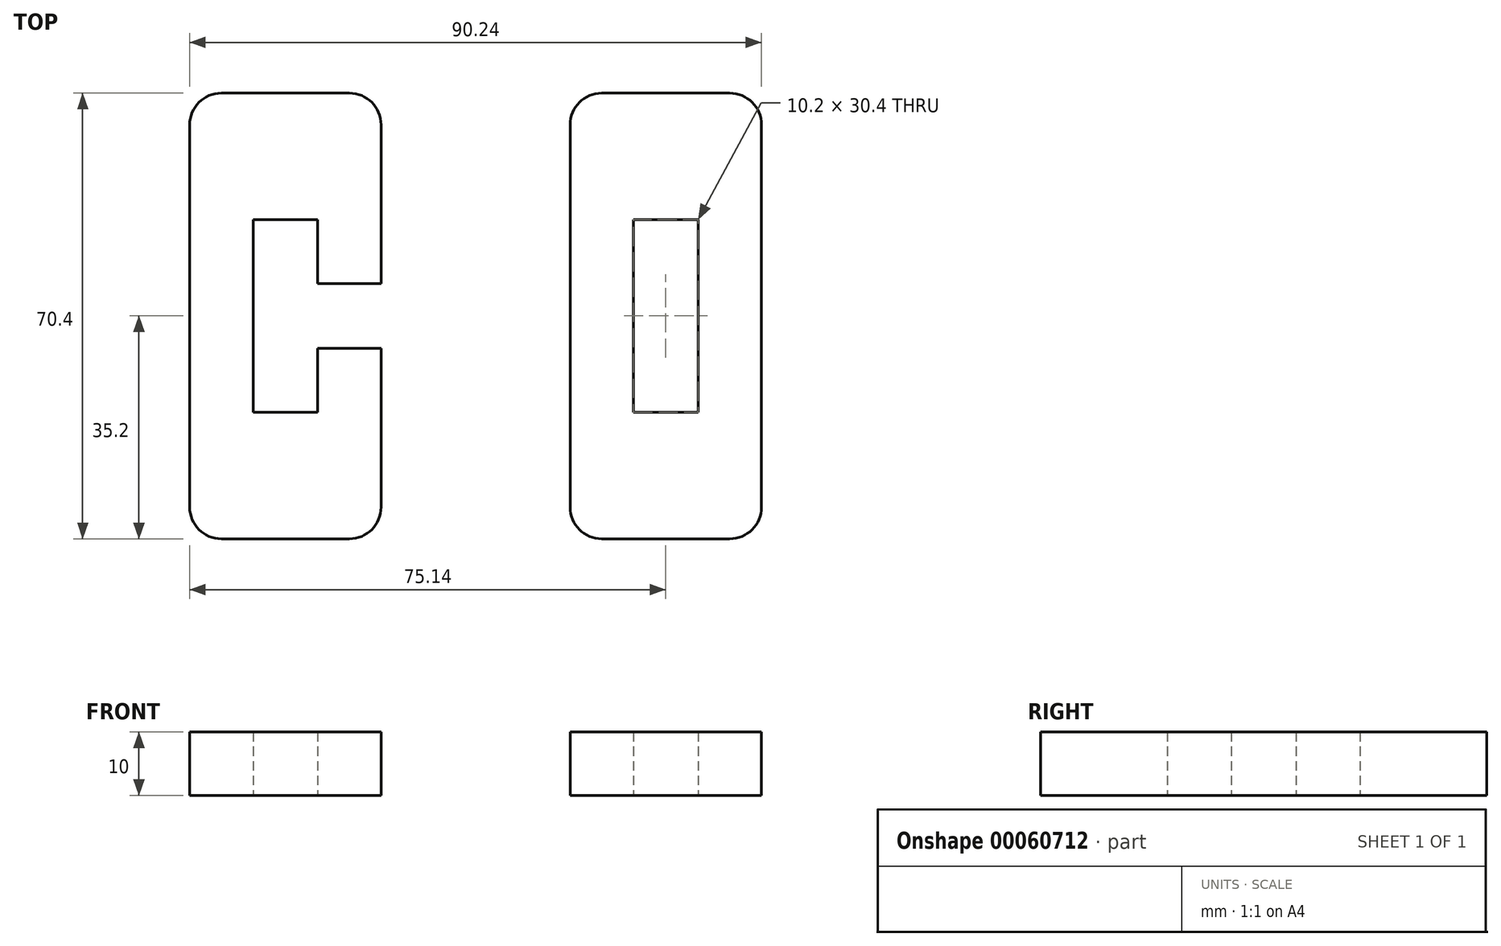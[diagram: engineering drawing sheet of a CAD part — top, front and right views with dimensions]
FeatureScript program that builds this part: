
annotation { "Feature Type Name" : "Feature", "Feature Type Description" : "" }
export const myFeature = defineFeature(function(context is Context, id is Id, definition is map)
    precondition{}
    {
        {
            var Q0;
            Q0=qCreatedBy(makeId("Top.planeOp"),FACE);
            var sketch = newSketch(context, id + "F0", { "sketchPlane" : qUnion([Q0])});
            skLineSegment(sketch, "E0.rect.bottom", {"start": v(-5.1, 15.2) * mm, "end": v(5.1, 15.2) * mm});
            skLineSegment(sketch, "E0.rect.top", {"start": v(-5.1, -15.2) * mm, "end": v(5.1, -15.2) * mm});
            skLineSegment(sketch, "E0.rect.left", {"start": v(-5.1, 15.2) * mm, "end": v(-5.1, -15.2) * mm});
            skLineSegment(sketch, "E0.rect.right", {"start": v(5.1, 15.2) * mm, "end": v(5.1, -15.2) * mm});
            skPoint(sketch, "E0.rect.middle", {"position": v(0, 0) * mm});
            skLineSegment(sketch, "E1.0", {"start": v(-10.1, 35.2) * mm, "end": v(10.1, 35.2) * mm});
            skLineSegment(sketch, "E1.1", {"start": v(-15.1, 30.2) * mm, "end": v(-15.1, -30.2) * mm});
            skLineSegment(sketch, "E1.2", {"start": v(-10.1, -35.2) * mm, "end": v(10.1, -35.2) * mm});
            skLineSegment(sketch, "E1.3", {"start": v(15.1, 30.2) * mm, "end": v(15.1, -30.2) * mm});
            skPoint(sketch, "E2", {"position": v(-60.04, 0) * mm});
            skLineSegment(sketch, "E3.rect.bottom", {"start": v(-65.14, 15.2) * mm, "end": v(-54.94, 15.2) * mm});
            skLineSegment(sketch, "E3.rect.top", {"start": v(-65.14, -15.2) * mm, "end": v(-54.94, -15.2) * mm});
            skLineSegment(sketch, "E3.rect.left", {"start": v(-65.14, 15.2) * mm, "end": v(-65.14, -15.2) * mm});
            skLineSegment(sketch, "E3.rect.right", {"start": v(-54.94, 15.2) * mm, "end": v(-54.94, -15.2) * mm});
            skLineSegment(sketch, "E4.0", {"start": v(-70.14, 35.2) * mm, "end": v(-49.94, 35.2) * mm});
            skLineSegment(sketch, "E4.1", {"start": v(-75.14, 30.2) * mm, "end": v(-75.14, -30.2) * mm});
            skLineSegment(sketch, "E4.2", {"start": v(-70.14, -35.2) * mm, "end": v(-49.94, -35.2) * mm});
            skLineSegment(sketch, "E4.3", {"start": v(-44.94, 30.2) * mm, "end": v(-44.94, -30.2) * mm});
            skLineSegment(sketch, "E5", {"start": v(-44.94, 0) * mm, "end": v(-54.94, 0) * mm});
            skLineSegment(sketch, "E6.0", {"start": v(-44.94, -5.1) * mm, "end": v(-54.94, -5.1) * mm});
            skLineSegment(sketch, "E7.0", {"start": v(-44.94, 5.1) * mm, "end": v(-54.94, 5.1) * mm});
            skPoint(sketch, "E8.visualSharp", {"position": v(-75.14, 35.2) * mm});
            skArc(sketch, "E8.filletArc", {"start": v(-70.14, 35.2) * mm, "mid": v(-73.68, 33.74) * mm, "end": v(-75.14, 30.2) * mm});
            skPoint(sketch, "E9.visualSharp", {"position": v(-44.94, 35.2) * mm});
            skArc(sketch, "E9.filletArc", {"start": v(-44.94, 30.2) * mm, "mid": v(-46.4, 33.74) * mm, "end": v(-49.94, 35.2) * mm});
            skPoint(sketch, "E10.visualSharp", {"position": v(-75.14, -35.2) * mm});
            skArc(sketch, "E10.filletArc", {"start": v(-75.14, -30.2) * mm, "mid": v(-73.68, -33.74) * mm, "end": v(-70.14, -35.2) * mm});
            skPoint(sketch, "E11.visualSharp", {"position": v(-44.94, -35.2) * mm});
            skArc(sketch, "E11.filletArc", {"start": v(-49.94, -35.2) * mm, "mid": v(-46.4, -33.74) * mm, "end": v(-44.94, -30.2) * mm});
            skPoint(sketch, "E12.visualSharp", {"position": v(-15.1, -35.2) * mm});
            skArc(sketch, "E12.filletArc", {"start": v(-15.1, -30.2) * mm, "mid": v(-13.64, -33.74) * mm, "end": v(-10.1, -35.2) * mm});
            skPoint(sketch, "E13.visualSharp", {"position": v(15.1, -35.2) * mm});
            skArc(sketch, "E13.filletArc", {"start": v(10.1, -35.2) * mm, "mid": v(13.64, -33.74) * mm, "end": v(15.1, -30.2) * mm});
            skPoint(sketch, "E14.visualSharp", {"position": v(-15.1, 35.2) * mm});
            skArc(sketch, "E14.filletArc", {"start": v(-10.1, 35.2) * mm, "mid": v(-13.64, 33.74) * mm, "end": v(-15.1, 30.2) * mm});
            skPoint(sketch, "E15.visualSharp", {"position": v(15.1, 35.2) * mm});
            skArc(sketch, "E15.filletArc", {"start": v(15.1, 30.2) * mm, "mid": v(13.64, 33.74) * mm, "end": v(10.1, 35.2) * mm});
            skSolve(sketch);
        }
        {
            var Q0;
            Q0=makeQuery(id+"F0.imprint","IMPRINT",FACE,{"disambiguationData":[TD([[makeQuery(id+"F0.imprint","IMPRINT",EDGE,{"derivedFrom":sQuery(id+"F0.wireOp",EDGE,"E0.rect.bottom")}),1.0]])]});
            var Q1;
            {var subQ3=sQuery(id+"F0.wireOp",EDGE,"E3.rect.bottom");Q1=makeQuery(id+"F0.imprint","IMPRINT",FACE,{"disambiguationData":[TD([[makeQuery(id+"F0.imprint","IMPRINT",EDGE,{"derivedFrom":subQ3}),1.0]])]});}
            extrude(context, id + "F1", {"entities" : qUnion([Q0, Q1]), "endBound" : BoundingType.SYMMETRIC, "depth" : 10 * mm});
        }
    });
